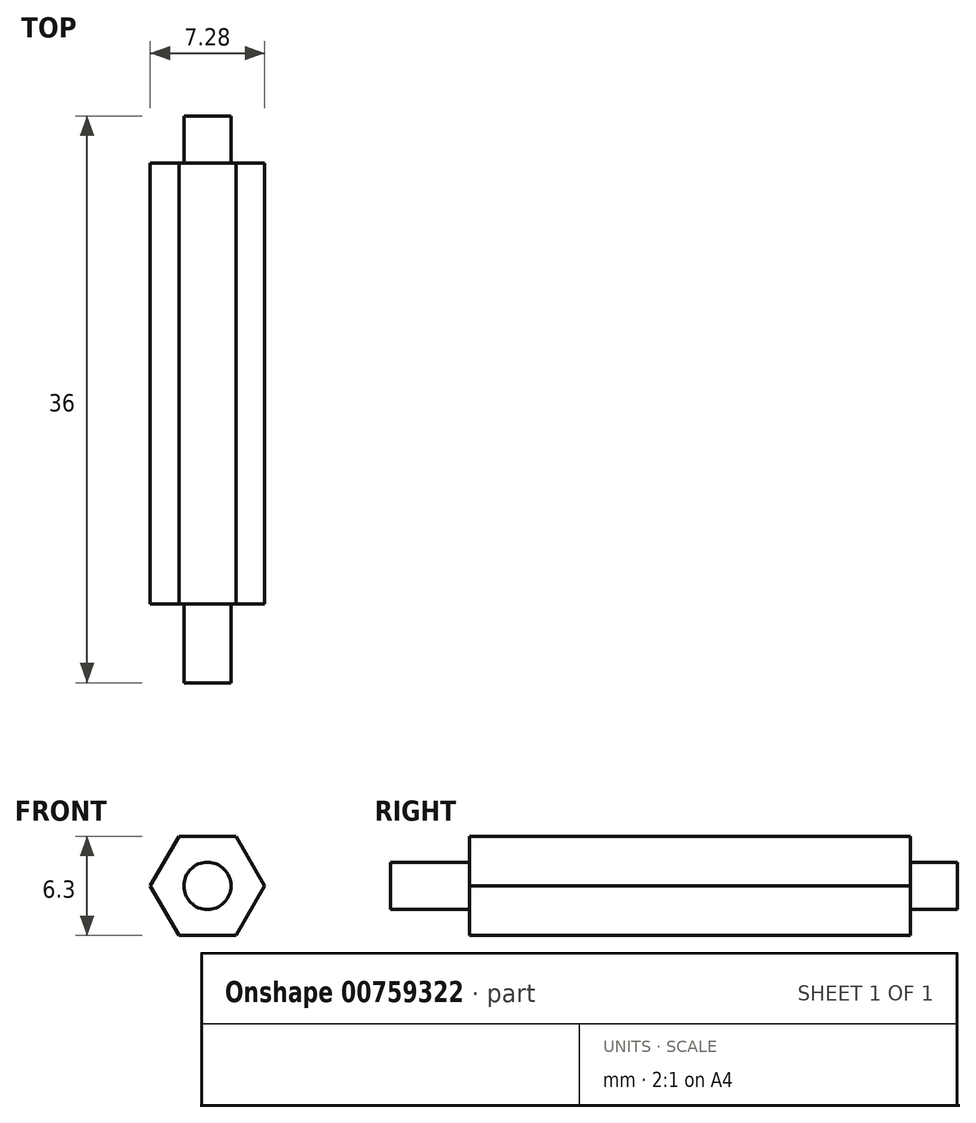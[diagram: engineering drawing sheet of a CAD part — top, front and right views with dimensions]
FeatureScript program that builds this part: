
annotation { "Feature Type Name" : "Feature", "Feature Type Description" : "" }
export const myFeature = defineFeature(function(context is Context, id is Id, definition is map)
    precondition{}
    {
        {
            var Q0;
            Q0=qCreatedBy(makeId("Front.planeOp"),FACE);
            var sketch = newSketch(context, id + "F0", { "sketchPlane" : qUnion([Q0])});
            skLineSegment(sketch, "E0", {"start": v(-1.06, -3.15) * mm, "end": v(2.58, -3.15) * mm});
            skLineSegment(sketch, "E1", {"start": v(2.58, -3.15) * mm, "end": v(4.4, 0) * mm});
            skLineSegment(sketch, "E2", {"start": v(4.4, 0) * mm, "end": v(2.58, 3.15) * mm});
            skLineSegment(sketch, "E3", {"start": v(2.58, 3.15) * mm, "end": v(-1.06, 3.15) * mm});
            skLineSegment(sketch, "E4", {"start": v(-1.06, 3.15) * mm, "end": v(-2.88, 0) * mm});
            skLineSegment(sketch, "E5", {"start": v(-2.88, 0) * mm, "end": v(-1.06, -3.15) * mm});
            skCircle(sketch, "E6", {"center": v(0.76, 0) * mm, "radius": 1.5 * mm});
            skSolve(sketch);
        }
        {
            var Q0;
            Q0=makeQuery(id+"F0.imprint","IMPRINT",FACE,{"disambiguationData":[TD([[makeQuery(id+"F0.imprint","IMPRINT",EDGE,{"derivedFrom":sQuery(id+"F0.wireOp",EDGE,"E0")}),1.0]])]});
            extrude(context, id + "F1", {"entities" : qUnion([Q0]), "endBound" : BoundingType.SYMMETRIC, "depth" : 28 * mm, "offsetDistance" : 25 * mm});
        }
        {
            var Q0;
            Q0=makeQuery(id+"F0.imprint","IMPRINT",FACE,{"disambiguationData":[TD([[makeQuery(id+"F0.imprint","IMPRINT",EDGE,{"derivedFrom":sQuery(id+"F0.wireOp",EDGE,"E6")}),1.0]])]});
            extrude(context, id + "F2", {"entities" : qUnion([Q0]), "operationType" : NewBodyOperationType.ADD, "depth" : 19 * mm, "offsetDistance" : 25 * mm});
        }
        {
            var Q0;
            Q0=makeQuery(id+"F0.imprint","IMPRINT",FACE,{"disambiguationData":[TD([[makeQuery(id+"F0.imprint","IMPRINT",EDGE,{"derivedFrom":sQuery(id+"F0.wireOp",EDGE,"E6")}),1.0]])]});
            extrude(context, id + "F3", {"entities" : qUnion([Q0]), "operationType" : NewBodyOperationType.ADD, "oppositeDirection" : true, "depth" : 17 * mm, "offsetDistance" : 25 * mm});
        }
    });
